# Revit family: Skyline Series Revit File_Sarkit
name_source: partatom
category: Lighting Fixtures
revit_build: Autodesk Revit 2017 (Build: 20160225_1515(x64)
units: mm (PartAtom-declared; Revit-internal decimal feet)

## family parameters
Cut with Voids When Loaded = Yes
Host = Face
Light Source = Yes
Part Type = Normal
Room Calculation Point = Yes
Round Connector Dimension = Use Diameter
Shared = Yes

## types (48) — shared parameters
Color Filter = 16777215
Default Elevation = 674 mm
Description = Skyline LED
Dimming Lamp Color Temperature Shift = <None>
Emit Shape Visible in Rendering = Yes
Emit from Rectangle Length = 1440 mm  [stored 4.72441 ft]
Emit from Rectangle Width = 65 mm  [stored 0.213255 ft]
Keynote = Continuous Lighting
Lamp = LED
Manufacturer = Arlight
Model = Skyline
Phase1 = Yes
Phase2 = No
Phase3 = No
Photometric Web File = generic
Suspenden Lenght = 500 mm  [stored 1.64042 ft]
Tilt Angle = 90.00°
URL = www.arlight.net/en/products/indoor-lighting/sykline
Voltage = 220-240V
zero-valued in all types: ref0

## per-type parameters (varying)
| type | Apparent Load | Diffuser Type | Type Comments | Type Image | Wattage Comments |
| SUSKL.35W.40.30 | 36 VA | Optic | Surface / Suspended Mounted | SU SKL.jpg | 35W |
| SUSKL.35W.30.30 | 36 VA | Optic | Surface / Suspended Mounted | SU SKL.jpg | 35W |
| SUSKL.35W.40.60 | 36 VA | Optic | Surface / Suspended Mounted | SU SKL.jpg | 35W |
| SUSKL.35W.30.60 | 36 VA | Optic | Surface / Suspended Mounted | SU SKL.jpg | 35W |
| SUSKL.58W.40.30 | 59 VA | Optic | Surface / Suspended Mounted | SU SKL.jpg | 58W |
| SUSKL.58W.30.30 | 59 VA | Optic | Surface / Suspended Mounted | SU SKL.jpg | 58W |
| SUSKL.58W.40.60 | 59 VA | Optic | Surface / Suspended Mounted | SU SKL.jpg | 58W |
| SUSKL.58W.30.60 | 59 VA | Optic | Surface / Suspended Mounted | SU SKL.jpg | 58W |
| SUSKL.35W.40.90 | 36 VA | Optic | Surface / Suspended Mounted | SU SKL.jpg | 35W |
| SUSKL.35W.30.90 | 36 VA | Optic | Surface / Suspended Mounted | SU SKL.jpg | 35W |
| SUSKL.35W.40.100/25 | 36 VA | Optic (Double Asymmetric) | Surface / Suspended Mounted | SU SKL.jpg | 35W |
| SUSKL.35W.30.100/25 | 36 VA | Optic (Double Asymmetric) | Surface / Suspended Mounted | SU SKL.jpg | 35W |
| SUSKL.58W.40.90 | 59 VA | Optic | Surface / Suspended Mounted | SU SKL.jpg | 58W |
| SUSKL.58W.30.90 | 59 VA | Optic | Surface / Suspended Mounted | SU SKL.jpg | 58W |
| SUSKL.58W.40.100/25 | 59 VA | Optic (Double Asymmetric) | Surface / Suspended Mounted | SU SKL.jpg | 58W |
| SUSKL.58W.30.100/25 | 59 VA | Optic (Double Asymmetric) | Surface / Suspended Mounted | SU SKL.jpg | 58W |
| SUSKL.35W.40.90/50 | 36 VA | Optic (Oval Distirbution) | Surface / Suspended Mounted | SU SKL.jpg | 35W |
| SUSKL.35W.30.90/50 | 36 VA | Optic (Oval Distirbution) | Surface / Suspended Mounted | SU SKL.jpg | 35W |
| SUSKL.58W.40.90/50 | 59 VA | Optic (Oval Distirbution) | Surface / Suspended Mounted | SU SKL.jpg | 58W |
| SUSKL.58W.30.90/50 | 59 VA | Optic (Oval Distirbution) | Surface / Suspended Mounted | SU SKL.jpg | 58W |
| SOSKL.35W.40.130 | 35 VA | Opal | Surface / Suspended Mounted | SO SKL.jpg | 35W |
| SOSKL.35W.30.130 | 35 VA | Opal | Surface / Suspended Mounted | SO SKL.jpg | 35W |
| SOSKL.51W.40.130 | 51 VA | Opal | Surface / Suspended Mounted | SO SKL.jpg | 54W |
| SOSKL.51W.30.130 | 51 VA | Opal | Surface / Suspended Mounted | SO SKL.jpg | 51W |
| SRSKR.35W.40.30 | 35 VA | Optic | Track Adapter | SR_SKL.jpg | 35W |
| SRSKR.35W.30.30 | 35 VA | Optic | Track Adapter | SR_SKL.jpg | 35W |
| SRSKR.35W.40.60 | 35 VA | Optic | Track Adapter | SR_SKL.jpg | 35W |
| SRSKR.35W.30.60 | 35 VA | Optic | Track Adapter | SR_SKL.jpg | 35W |
| SRSKR.58W.40.30 | 59 VA | Optic | Track Adapter | SR_SKL.jpg | 58W |
| SRSKR.58W.30.30 | 59 VA | Optic | Track Adapter | SR_SKL.jpg | 58W |
| SRSKR.58W.40.60 | 59 VA | Optic | Track Adapter | SR_SKL.jpg | 58W |
| SRSKR.58W.30.60 | 59 VA | Optic | Track Adapter | SR_SKL.jpg | 58W |
| SRSKR.35W.40.90 | 35 VA | Optic | Track Adapter | SR_SKL.jpg | 35W |
| SRSKR.35W.30.90 | 35 VA | Optic | Track Adapter | SR_SKL.jpg | 35W |
| SRSKR.35W.40.100/25 | 35 VA | Optic (Double Asymmetric) | Track Adapter | SU SKL.jpg | 35W |
| SRSKR.35W.30.100/25 | 35 VA | Optic (Double Asymmetric) | Track Adapter | SU SKL.jpg | 35W |
| SRSKR.58W.40.90 | 59 VA | Optic | Track Adapter | SR_SKL.jpg | 58W |
| SRSKR.58W.30.90 | 59 VA | Optic | Track Adapter | SR_SKL.jpg | 58W |
| SRSKR.58W.40.100/25 | 59 VA | Optic (Double Asymmetric) | Track Adapter | SU SKL.jpg | 58W |
| SRSKR.58W.30.100/25 | 59 VA | Optic (Double Asymmetric) | Track Adapter | SU SKL.jpg | 58W |
| SRSKR.35W.40.90/50 | 35 VA | Optic (Oval Distirbution) | Track Adapter | SR_SKL.jpg | 35W |
| SRSKR.35W.30.90/50 | 35 VA | Optic (Oval Distirbution) | Track Adapter | SR_SKL.jpg | 35W |
| SRSKR.58W.40.90/50 | 59 VA | Optic (Oval Distirbution) | Track Adapter | SR_SKL.jpg | 58W |
| SRSKR.58W.30.90/50 | 59 VA | Optic (Oval Distirbution) | Track Adapter | SR_SKL.jpg | 58W |
| SOSKR.35W.40.130 | 35 VA | Opal | Track Adapter | SO_SKR.jpg | 35W |
| SOSKR.35W.30.130 | 35 VA | Opal | Track Adapter | SO_SKR.jpg | 35W |
| SOSKR.51W.40.130 | 51 VA | Opal | Track Adapter | SO_SKR.jpg | 54 |
| SOSKR.51W.30.130 | 51 VA | Opal | Track Adapter | SO_SKR.jpg | 51W |

note: [stored X ft] marks values corroborated as IEEE doubles in the binary element streams (Revit-internal decimal feet)

## geometry (parser evidence)
native form markers: Blend x4, Sweep x3
no freeform markers — native parametric forms only
